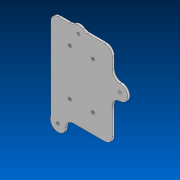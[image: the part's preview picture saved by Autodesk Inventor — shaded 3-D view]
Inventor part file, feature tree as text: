
AUTODESK INVENTOR PART (.ipt)
format: ipt  version: 2022 (Build 260153000, 153)  size: 130,560 bytes
history: native  units: in
note: dims shown in document units (in); Inventor stores cm internally (conversion verified against a paired STEP export)
features: extrude x1, hole x1
ambient origin geometry x8: Origin, YZ Plane, XZ Plane, XY Plane, X Axis, Y Axis, Z Axis, Center Point
bodies: Solid1 (feature_tree)
feature tree (2):
  extrude  "Extrusion1"  Depth=1.5in
  hole  "Hole1"  [1 undecoded]
note: 1 required parameter value undecoded (feature->parameter linkage not recoverable at this tier; creation-order binding heuristic only, values carry confidence <= 0.55)
